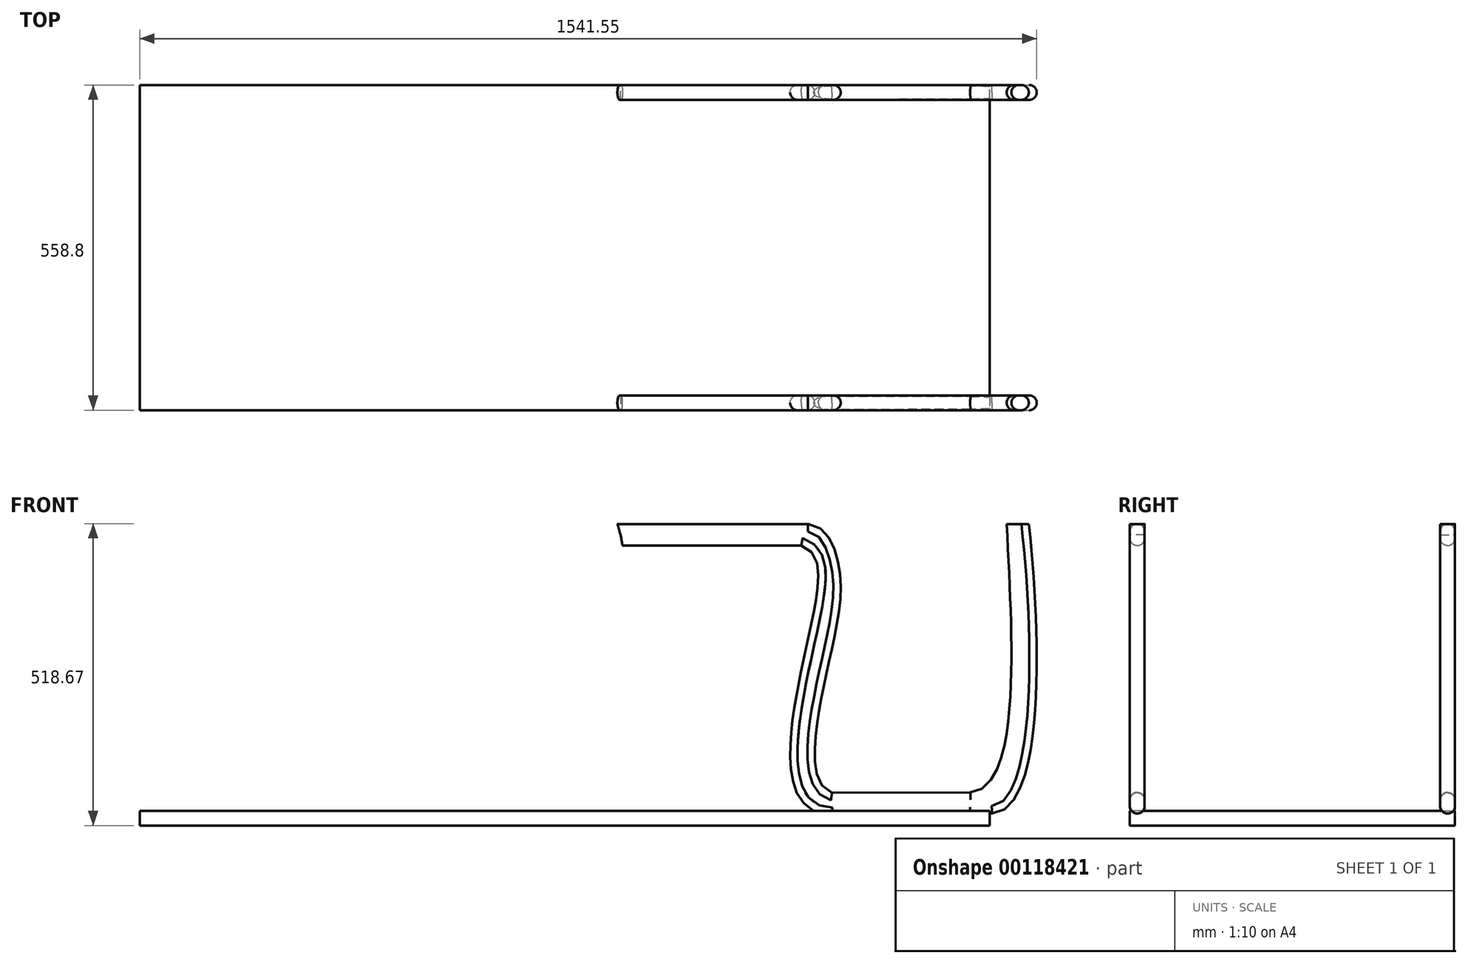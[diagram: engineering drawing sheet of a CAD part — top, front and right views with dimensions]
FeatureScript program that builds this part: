
annotation { "Feature Type Name" : "Feature", "Feature Type Description" : "" }
export const myFeature = defineFeature(function(context is Context, id is Id, definition is map)
    precondition{}
    {
        {
            var Q0;
            Q0=qCreatedBy(makeId("Front.planeOp"),FACE);
            var sketch = newSketch(context, id + "F0", { "sketchPlane" : qUnion([Q0])});
            skLineSegment(sketch, "E0", {"start": v(864.68, 18.01) * mm, "end": v(1102.26, 19.05) * mm});
            skLineSegment(sketch, "E1", {"start": v(811.67, 481) * mm, "end": v(504.48, 481) * mm});
            skFitSpline(sketch, "E2", {"points": [v(504.48, 481) * mm, v(-275.7, 19.05) * mm], "startDerivative": vector(-878.83, -151.3) * mm, "endDerivative": vector(-678.72, -646.09) * mm});
            skLineSegment(sketch, "E3", {"start": v(1102.26, 19.05) * mm, "end": v(1139.3, 20.75) * mm});
            skFitSpline(sketch, "E4.0", {"points": [v(498.01, 518.54) * mm, v(459.83, 511.97) * mm, v(384.63, 494.1) * mm, v(275.53, 454.8) * mm, v(170.13, 404.67) * mm, v(68.42, 345.35) * mm, v(-29.67, 278.39) * mm, v(-155.66, 180.97) * mm, v(-244.85, 101.02) * mm, v(-301.96, 46.65) * mm]});
            skLineSegment(sketch, "E5.0", {"start": v(864.47, 56.11) * mm, "end": v(1102.09, 57.15) * mm});
            skLineSegment(sketch, "E6", {"start": v(495.67, 518.14) * mm, "end": v(823.38, 518.14) * mm});
            skLineSegment(sketch, "E7", {"start": v(-301.96, 46.65) * mm, "end": v(-328.52, 19.25) * mm});
            skLineSegment(sketch, "E8", {"start": v(-328.52, 19.25) * mm, "end": v(-275.7, 19.05) * mm});
            skLineSegment(sketch, "E9", {"start": v(504.48, 481) * mm, "end": v(501.21, 499.76) * mm});
            skLineSegment(sketch, "E10", {"start": v(495.67, 518.14) * mm, "end": v(501.21, 499.76) * mm});
            skLineSegment(sketch, "E11", {"start": v(811.67, 481) * mm, "end": v(823.38, 518.14) * mm});
            skLineSegment(sketch, "E12", {"start": v(864.68, 18.01) * mm, "end": v(864.47, 56.11) * mm});
            skFitSpline(sketch, "E13", {"points": [v(823.38, 518.14) * mm, v(876.86, 441.33) * mm, v(860.95, 289) * mm, v(864.47, 56.11) * mm], "startDerivative": vector(389.43, -30.07) * mm, "endDerivative": vector(390.36, -118.08) * mm});
            skFitSpline(sketch, "E14", {"points": [v(811.67, 481) * mm, v(840.75, 420.5) * mm, v(864.68, 18.01) * mm], "startDerivative": vector(170.59, -60.1) * mm, "endDerivative": vector(604.44, -16.98) * mm});
            skFitSpline(sketch, "E15", {"points": [v(1202.68, 518.03) * mm, v(1139.3, 20.75) * mm], "startDerivative": vector(64.78, -570.92) * mm, "endDerivative": vector(-275, -6.95) * mm});
            skLineSegment(sketch, "E16", {"start": v(1202.68, 518.03) * mm, "end": v(1164.58, 518.03) * mm});
            skFitSpline(sketch, "E17", {"points": [v(1164.58, 518.03) * mm, v(1102.09, 57.15) * mm], "startDerivative": vector(29.3, -576.77) * mm, "endDerivative": vector(-269.48, -14.94) * mm});
            skSolve(sketch);
        }
        {
            var Q0;
            Q0 = qSketchRegion(id + "F0", true);
            extrude(context, id + "F1", {"entities" : qUnion([Q0]), "depth" : 25.4 * mm});
        }
        {
            var Q0;
            Q0=makeQuery(id+"F1.opExtrude","CAP_EDGE",EDGE,{"disambiguationData":[OSD([sQuery(id+"F0.wireOp",EDGE,"E6")])],"isStart":false});
            var Q1;
            Q1=makeQuery(id+"F1.opExtrude","CAP_EDGE",EDGE,{"disambiguationData":[OSD([sQuery(id+"F0.wireOp",EDGE,"E6")])],"isStart":true});
            var Q2;
            Q2=makeQuery(id+"F1.opExtrude","CAP_EDGE",EDGE,{"disambiguationData":[OSD([sQuery(id+"F0.wireOp",EDGE,"E1")])],"isStart":false});
            var Q3;
            Q3=makeQuery(id+"F1.opExtrude","CAP_EDGE",EDGE,{"disambiguationData":[OSD([sQuery(id+"F0.wireOp",EDGE,"E4.0")])],"isStart":false});
            var Q4;
            Q4=makeQuery(id+"F1.opExtrude","CAP_EDGE",EDGE,{"disambiguationData":[OSD([sQuery(id+"F0.wireOp",EDGE,"E2")])],"isStart":false});
            var Q5;
            Q5=makeQuery(id+"F1.opExtrude","CAP_EDGE",EDGE,{"disambiguationData":[OSD([sQuery(id+"F0.wireOp",EDGE,"E4.0")])],"isStart":true});
            var Q6;
            Q6=makeQuery(id+"F1.opExtrude","CAP_EDGE",EDGE,{"disambiguationData":[OSD([sQuery(id+"F0.wireOp",EDGE,"E2")])],"isStart":true});
            fillet(context, id + "F2", {"entities" : qUnion([Q0, Q1, Q2, Q3, Q4, Q5, Q6]), "radius" : 12.7 * mm, "tangentPropagation" : true, "allowEdgeOverflow" : false});
        }
        {
            var Q0;
            Q0=makeQuery(id+"F1.opExtrude","CAP_EDGE",EDGE,{"disambiguationData":[OSD([sQuery(id+"F0.wireOp",EDGE,"E13")])],"isStart":false});
            var Q1;
            Q1=makeQuery(id+"F1.opExtrude","CAP_EDGE",EDGE,{"disambiguationData":[OSD([sQuery(id+"F0.wireOp",EDGE,"87527852-a6e2-4d8d-ab23-b79fd36443ad")])],"isStart":false});
            var Q2;
            Q2=makeQuery(id+"F1.opExtrude","CAP_EDGE",EDGE,{"disambiguationData":[OSD([sQuery(id+"F0.wireOp",EDGE,"E14")])],"isStart":false});
            var Q3;
            Q3=makeQuery(id+"F1.opExtrude","CAP_EDGE",EDGE,{"disambiguationData":[OSD([sQuery(id+"F0.wireOp",EDGE,"E14")])],"isStart":true});
            var Q4;
            Q4=makeQuery(id+"F1.opExtrude","CAP_EDGE",EDGE,{"disambiguationData":[OSD([sQuery(id+"F0.wireOp",EDGE,"E13")])],"isStart":true});
            var Q5;
            Q5=makeQuery(id+"F1.opExtrude","CAP_EDGE",EDGE,{"disambiguationData":[OSD([sQuery(id+"F0.wireOp",EDGE,"E1")])],"isStart":true});
            var Q6;
            Q6=makeQuery(id+"F1.opExtrude","CAP_EDGE",EDGE,{"disambiguationData":[OSD([sQuery(id+"F0.wireOp",EDGE,"E5.0")])],"isStart":false});
            var Q7;
            Q7=makeQuery(id+"F1.opExtrude","CAP_EDGE",EDGE,{"disambiguationData":[OSD([sQuery(id+"F0.wireOp",EDGE,"E0")])],"isStart":true});
            var Q8;
            Q8=makeQuery(id+"F1.opExtrude","CAP_EDGE",EDGE,{"disambiguationData":[OSD([sQuery(id+"F0.wireOp",EDGE,"E5.0")])],"isStart":true});
            var Q9;
            Q9=makeQuery(id+"F1.opExtrude","CAP_EDGE",EDGE,{"disambiguationData":[OSD([sQuery(id+"F0.wireOp",EDGE,"E0")])],"isStart":false});
            var Q10;
            Q10=makeQuery(id+"F1.opExtrude","CAP_EDGE",EDGE,{"disambiguationData":[OSD([sQuery(id+"F0.wireOp",EDGE,"E15")])],"isStart":false});
            var Q11;
            Q11=makeQuery(id+"F1.opExtrude","CAP_EDGE",EDGE,{"disambiguationData":[OSD([sQuery(id+"F0.wireOp",EDGE,"E17")])],"isStart":false});
            var Q12;
            Q12=makeQuery(id+"F1.opExtrude","CAP_EDGE",EDGE,{"disambiguationData":[OSD([sQuery(id+"F0.wireOp",EDGE,"E15")])],"isStart":true});
            var Q13;
            Q13=makeQuery(id+"F1.opExtrude","CAP_EDGE",EDGE,{"disambiguationData":[OSD([sQuery(id+"F0.wireOp",EDGE,"E17")])],"isStart":true});
            fillet(context, id + "F3", {"entities" : qUnion([Q0, Q1, Q2, Q3, Q4, Q5, Q6, Q7, Q8, Q9, Q10, Q11, Q12, Q13]), "radius" : 12.7 * mm, "tangentPropagation" : true, "allowEdgeOverflow" : false});
        }
        {
            var Q0;
            Q0=qCreatedBy(makeId("Top.planeOp"),FACE);
            var sketch = newSketch(context, id + "F4", { "sketchPlane" : qUnion([Q0])});
            skLineSegment(sketch, "E18.bottom", {"start": v(-325.24, 0) * mm, "end": v(1135.26, 0) * mm});
            skLineSegment(sketch, "E18.top", {"start": v(-325.24, -279.4) * mm, "end": v(1135.26, -279.4) * mm});
            skLineSegment(sketch, "E18.left", {"start": v(-325.24, 0) * mm, "end": v(-325.24, -279.4) * mm});
            skLineSegment(sketch, "E18.right", {"start": v(1135.26, 0) * mm, "end": v(1135.26, -279.4) * mm});
            skSolve(sketch);
        }
        {
            var Q0;
            Q0=makeQuery(id+"F4.imprint","IMPRINT",FACE,{"disambiguationData":[TD([[makeQuery(id+"F4.imprint","IMPRINT",EDGE,{"derivedFrom":sQuery(id+"F4.wireOp",EDGE,"E18.bottom")}),-1.0]])]});
            extrude(context, id + "F5", {"entities" : qUnion([Q0]), "operationType" : NewBodyOperationType.ADD, "depth" : 25.4 * mm});
        }
        {
            var Q0;
            Q0=makeQuery(id+"F1.opExtrude","SWEPT_BODY",BODY,{"disambiguationData":[OSD([sQuery(id+"F0.wireOp",EDGE,"E1"),sQuery(id+"F0.wireOp",EDGE,"E2"),sQuery(id+"F0.wireOp",EDGE,"E0"),sQuery(id+"F0.wireOp",EDGE,"E3"),sQuery(id+"F0.wireOp",EDGE,"E4.0"),sQuery(id+"F0.wireOp",EDGE,"E5.0"),sQuery(id+"F0.wireOp",EDGE,"E6"),sQuery(id+"F0.wireOp",EDGE,"E7"),sQuery(id+"F0.wireOp",EDGE,"E8"),sQuery(id+"F0.wireOp",EDGE,"E13"),sQuery(id+"F0.wireOp",EDGE,"E14"),sQuery(id+"F0.wireOp",EDGE,"E15"),sQuery(id+"F0.wireOp",EDGE,"E16"),sQuery(id+"F0.wireOp",EDGE,"E17")])]});
            var Q1;
            Q1=makeQuery(id+"F5.opExtrude","SWEPT_FACE",FACE,{"disambiguationData":[OSD([sQuery(id+"F4.wireOp",EDGE,"E18.top")])]});
            mirror(context, id + "F6", {"operationType" : NewBodyOperationType.ADD, "entities" : qUnion([Q0]), "mirrorPlane" : qUnion([Q1])});
        }
    });
